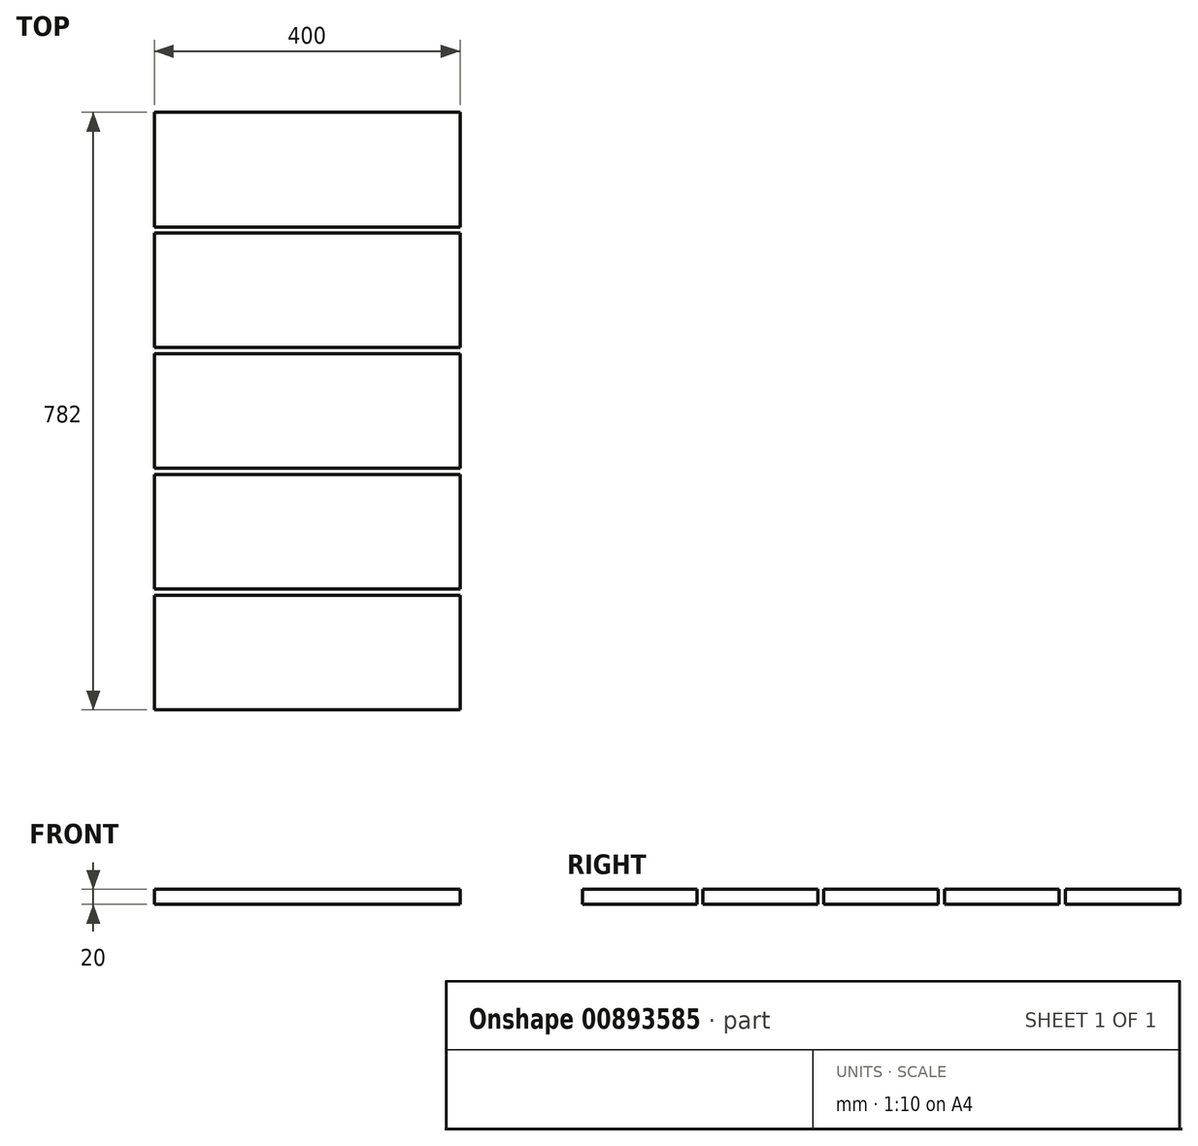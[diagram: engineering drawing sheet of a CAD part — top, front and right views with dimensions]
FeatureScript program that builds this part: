
annotation { "Feature Type Name" : "Feature", "Feature Type Description" : "" }
export const myFeature = defineFeature(function(context is Context, id is Id, definition is map)
    precondition{}
    {
        {
            var Q0;
            Q0=qCreatedBy(makeId("Top.planeOp"),FACE);
            var sketch = newSketch(context, id + "F0", { "sketchPlane" : qUnion([Q0])});
            skLineSegment(sketch, "E0.bottom", {"start": v(0, 0) * mm, "end": v(-400, 0) * mm});
            skLineSegment(sketch, "E0.top", {"start": v(0, 150) * mm, "end": v(-400, 150) * mm});
            skLineSegment(sketch, "E0.left", {"start": v(0, 0) * mm, "end": v(0, 150) * mm});
            skLineSegment(sketch, "E0.right", {"start": v(-400, 0) * mm, "end": v(-400, 150) * mm});
            skLineSegment(sketch, "E1.0.1.0", {"start": v(0, 308) * mm, "end": v(-400, 308) * mm});
            skLineSegment(sketch, "E1.0.1.1", {"start": v(0, 158) * mm, "end": v(-400, 158) * mm});
            skLineSegment(sketch, "E1.0.1.2", {"start": v(0, 158) * mm, "end": v(0, 308) * mm});
            skLineSegment(sketch, "E1.0.1.3", {"start": v(-400, 158) * mm, "end": v(-400, 308) * mm});
            skLineSegment(sketch, "E1.0.2.0", {"start": v(0, 466) * mm, "end": v(-400, 466) * mm});
            skLineSegment(sketch, "E1.0.2.1", {"start": v(0, 316) * mm, "end": v(-400, 316) * mm});
            skLineSegment(sketch, "E1.0.2.2", {"start": v(0, 316) * mm, "end": v(0, 466) * mm});
            skLineSegment(sketch, "E1.0.2.3", {"start": v(-400, 316) * mm, "end": v(-400, 466) * mm});
            skLineSegment(sketch, "E1.0.3.0", {"start": v(0, 624) * mm, "end": v(-400, 624) * mm});
            skLineSegment(sketch, "E1.0.3.1", {"start": v(0, 474) * mm, "end": v(-400, 474) * mm});
            skLineSegment(sketch, "E1.0.3.2", {"start": v(0, 474) * mm, "end": v(0, 624) * mm});
            skLineSegment(sketch, "E1.0.3.3", {"start": v(-400, 474) * mm, "end": v(-400, 624) * mm});
            skLineSegment(sketch, "E1.0.4.0", {"start": v(0, 782) * mm, "end": v(-400, 782) * mm});
            skLineSegment(sketch, "E1.0.4.1", {"start": v(0, 632) * mm, "end": v(-400, 632) * mm});
            skLineSegment(sketch, "E1.0.4.2", {"start": v(0, 632) * mm, "end": v(0, 782) * mm});
            skLineSegment(sketch, "E1.0.4.3", {"start": v(-400, 632) * mm, "end": v(-400, 782) * mm});
            skLineSegment(sketch, "E1.direction1", {"start": v(-775, 150) * mm, "end": v(-400, 150) * mm, "construction": true});
            skLineSegment(sketch, "E1.direction2", {"start": v(-400, 150) * mm, "end": v(-400, 308) * mm, "construction": true});
            skSolve(sketch);
        }
        {
            var Q0;
            Q0 = qSketchRegion(id + "F0", true);
            extrude(context, id + "F1", {"entities" : qUnion([Q0]), "depth" : 20 * mm, "offsetDistance" : 25 * mm});
        }
    });
